annotation { "Feature Type Name" : "Feature", "Feature Type Description" : "" }
export const myFeature = defineFeature(function(context is Context, id is Id, definition is map)
    precondition{}
    {
        {
            var Q0;
            Q0=qCreatedBy(makeId("Top.planeOp"),FACE);
            var sketch = newSketch(context, id + "F0", { "sketchPlane" : qUnion([Q0])});
            skLineSegment(sketch, "E0", {"start": v(-20.99, 34.78) * mm, "end": v(18.62, 34.78) * mm});
            skLineSegment(sketch, "E1", {"start": v(18.62, 34.78) * mm, "end": v(33.2, 0) * mm});
            skLineSegment(sketch, "E2", {"start": v(33.2, 0) * mm, "end": v(18.62, -33.2) * mm});
            skLineSegment(sketch, "E3", {"start": v(18.62, -33.2) * mm, "end": v(-20.99, -33.2) * mm});
            skLineSegment(sketch, "E4", {"start": v(-20.99, -33.2) * mm, "end": v(-37.34, 0) * mm});
            skLineSegment(sketch, "E5", {"start": v(-37.34, 0) * mm, "end": v(-20.99, 34.78) * mm});
            skSolve(sketch);
        }
        {
            var Q0;
            Q0 = qSketchRegion(id + "F0", true);
            extrude(context, id + "F1", {"entities" : qUnion([Q0]), "depth" : 17.27 * mm, "offsetDistance" : 25.4 * mm});
        }
        {
            var Q0;
            Q0=makeQuery(id+"F1.opExtrude","CAP_FACE",FACE,{"disambiguationData":[OSD([sQuery(id+"F0.wireOp",EDGE,"E0"),sQuery(id+"F0.wireOp",EDGE,"E1"),sQuery(id+"F0.wireOp",EDGE,"E2"),sQuery(id+"F0.wireOp",EDGE,"E3"),sQuery(id+"F0.wireOp",EDGE,"E4"),sQuery(id+"F0.wireOp",EDGE,"E5")])],"isStart":false});
            var sketch = newSketch(context, id + "F2", { "sketchPlane" : qUnion([Q0])});
            skCircle(sketch, "E6", {"center": v(0, 0) * mm, "radius": 10.81 * mm});
            skSolve(sketch);
        }
        {
            var Q0;
            Q0 = qSketchRegion(id + "F2", true);
            extrude(context, id + "F3", {"entities" : qUnion([Q0]), "operationType" : NewBodyOperationType.ADD, "depth" : 33.53 * mm, "offsetDistance" : 25.4 * mm});
        }
        {
            var Q0;
            Q0=qCreatedBy(makeId("Front.planeOp"),FACE);
            var sketch = newSketch(context, id + "F4", { "sketchPlane" : qUnion([Q0])});
            skText(sketch, "E7", { "text": "NATRACK&FEILD\n", "fontName": "Tinos-Regular.ttf"});
            const initialGuessF4  = {"E7": [-0.0672, 0.05094, 1, 0, 0.01143]};
            skSetInitialGuess(sketch, initialGuessF4);
            skSolve(sketch);
        }
        {
            var Q0;
            Q0=qCreatedBy(makeId("Front.planeOp"),FACE);
            var sketch = newSketch(context, id + "F5", { "sketchPlane" : qUnion([Q0])});
            skText(sketch, "E8", { "text": "BEAU BERNADEAU\n", "fontName": "RobotoSlab-Regular.ttf"});
            const initialGuessF5  = {"E8": [-0.06208, 0.01764, 1, 0, 0.00946]};
            skSetInitialGuess(sketch, initialGuessF5);
            skSolve(sketch);
        }
        {
            var Q0;
            Q0 = qSketchRegion(id + "F5", true);
            extrude(context, id + "F6", {"entities" : qUnion([Q0]), "operationType" : NewBodyOperationType.ADD, "depth" : 25.4 * mm, "offsetDistance" : 25.4 * mm});
        }
        {
            var Q0;
            Q0=qCreatedBy(makeId("Top.planeOp"),FACE);
            var sketch = newSketch(context, id + "F7", { "sketchPlane" : qUnion([Q0])});
            skLineSegment(sketch, "E9", {"start": v(29.37, -30.26) * mm, "end": v(68.3, -30.26) * mm});
            skLineSegment(sketch, "E10", {"start": v(68.3, -30.26) * mm, "end": v(68.3, -5.6) * mm});
            skLineSegment(sketch, "E11", {"start": v(68.3, -5.6) * mm, "end": v(39.65, -5.6) * mm});
            skLineSegment(sketch, "E12", {"start": v(29.37, -30.26) * mm, "end": v(22.7, -24.06) * mm});
            skLineSegment(sketch, "E13", {"start": v(22.7, -24.06) * mm, "end": v(29.37, -4.19) * mm});
            skLineSegment(sketch, "E14", {"start": v(29.37, -4.19) * mm, "end": v(39.65, -5.6) * mm});
            skSolve(sketch);
        }
        {
            var Q0;
            Q0 = qSketchRegion(id + "F7", true);
            extrude(context, id + "F8", {"entities" : qUnion([Q0]), "operationType" : NewBodyOperationType.ADD, "depth" : 17.27 * mm, "offsetDistance" : 25.4 * mm});
        }
        {
            var Q0;
            Q0=qCreatedBy(makeId("Top.planeOp"),FACE);
            var sketch = newSketch(context, id + "F9", { "sketchPlane" : qUnion([Q0])});
            skLineSegment(sketch, "E15", {"start": v(-24.93, -25.91) * mm, "end": v(-61, -25.91) * mm});
            skLineSegment(sketch, "E16", {"start": v(-61, -25.91) * mm, "end": v(-61, 0) * mm});
            skLineSegment(sketch, "E17", {"start": v(-61, 0) * mm, "end": v(-36.95, 0) * mm});
            skLineSegment(sketch, "E18", {"start": v(-36.95, 0) * mm, "end": v(-24.93, -25.91) * mm});
            skSolve(sketch);
        }
        {
            var Q0;
            Q0 = qSketchRegion(id + "F9", true);
            extrude(context, id + "F10", {"entities" : qUnion([Q0]), "depth" : 17.78 * mm, "offsetDistance" : 25.4 * mm});
        }
        {
            var Q0;
            Q0 = qSketchRegion(id + "F4", true);
            extrude(context, id + "F11", {"entities" : qUnion([Q0]), "operationType" : NewBodyOperationType.REMOVE, "depth" : 6.6 * mm, "offsetDistance" : 25.4 * mm});
        }
    });